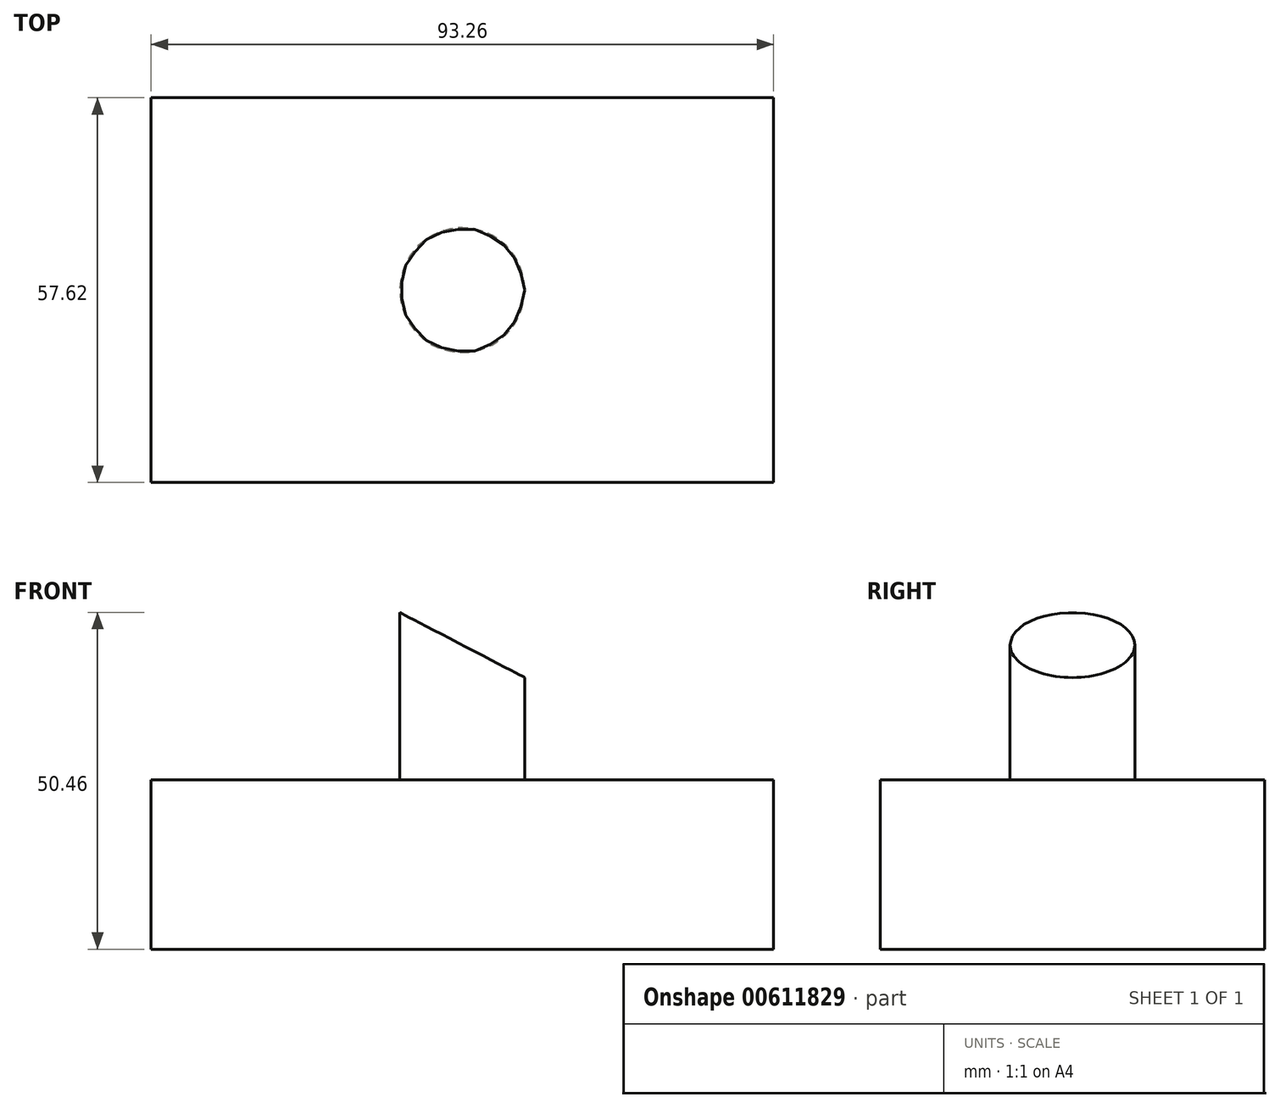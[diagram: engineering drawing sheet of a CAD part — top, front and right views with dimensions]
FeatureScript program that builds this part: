
annotation { "Feature Type Name" : "Feature", "Feature Type Description" : "" }
export const myFeature = defineFeature(function(context is Context, id is Id, definition is map)
    precondition{}
    {
        {
            var Q0;
            Q0=qCreatedBy(makeId("Top.planeOp"),FACE);
            var sketch = newSketch(context, id + "F0", { "sketchPlane" : qUnion([Q0])});
            skLineSegment(sketch, "E0.bottom", {"start": v(-46.63, 28.81) * mm, "end": v(46.63, 28.81) * mm});
            skLineSegment(sketch, "E0.top", {"start": v(-46.63, -28.81) * mm, "end": v(46.63, -28.81) * mm});
            skLineSegment(sketch, "E0.left", {"start": v(-46.63, 28.81) * mm, "end": v(-46.63, -28.81) * mm});
            skLineSegment(sketch, "E0.right", {"start": v(46.63, 28.81) * mm, "end": v(46.63, -28.81) * mm});
            skPoint(sketch, "E0.middle", {"position": v(0, 0) * mm});
            skCircle(sketch, "E1", {"center": v(0, 0) * mm, "radius": 9.35 * mm});
            skSolve(sketch);
        }
        {
            var Q0;
            Q0=makeQuery(id+"F0.imprint","IMPRINT",FACE,{"disambiguationData":[TD([[makeQuery(id+"F0.imprint","IMPRINT",EDGE,{"derivedFrom":sQuery(id+"F0.wireOp",EDGE,"E1")}),1.0]])]});
            extrude(context, id + "F1", {"entities" : qUnion([Q0]), "depth" : 50.8 * mm, "offsetDistance" : 25.4 * mm});
        }
        {
            var Q0;
            Q0 = qSketchRegion(id + "F0", true);
            extrude(context, id + "F2", {"entities" : qUnion([Q0]), "operationType" : NewBodyOperationType.ADD, "depth" : 25.4 * mm, "offsetDistance" : 25.4 * mm});
        }
        {
            var Q0;
            Q0=qCreatedBy(makeId("Front.planeOp"),FACE);
            var sketch = newSketch(context, id + "F3", { "sketchPlane" : qUnion([Q0])});
            skLineSegment(sketch, "E2", {"start": v(-13.47, 52.6) * mm, "end": v(29.05, 52.6) * mm});
            skLineSegment(sketch, "E3", {"start": v(-13.47, 52.6) * mm, "end": v(29.05, 30.43) * mm});
            skLineSegment(sketch, "E4", {"start": v(29.05, 30.43) * mm, "end": v(29.05, 52.6) * mm});
            skSolve(sketch);
        }
        {
            var Q0;
            Q0 = qSketchRegion(id + "F3", true);
            extrude(context, id + "F4", {"entities" : qUnion([Q0]), "operationType" : NewBodyOperationType.REMOVE, "oppositeDirection" : true, "depth" : 25.4 * mm, "offsetDistance" : 25.4 * mm});
        }
        {
            var Q0;
            Q0 = qSketchRegion(id + "F3", true);
            extrude(context, id + "F5", {"entities" : qUnion([Q0]), "operationType" : NewBodyOperationType.REMOVE, "oppositeDirection" : true, "depth" : -76.2 * mm, "offsetDistance" : 25.4 * mm});
        }
    });
